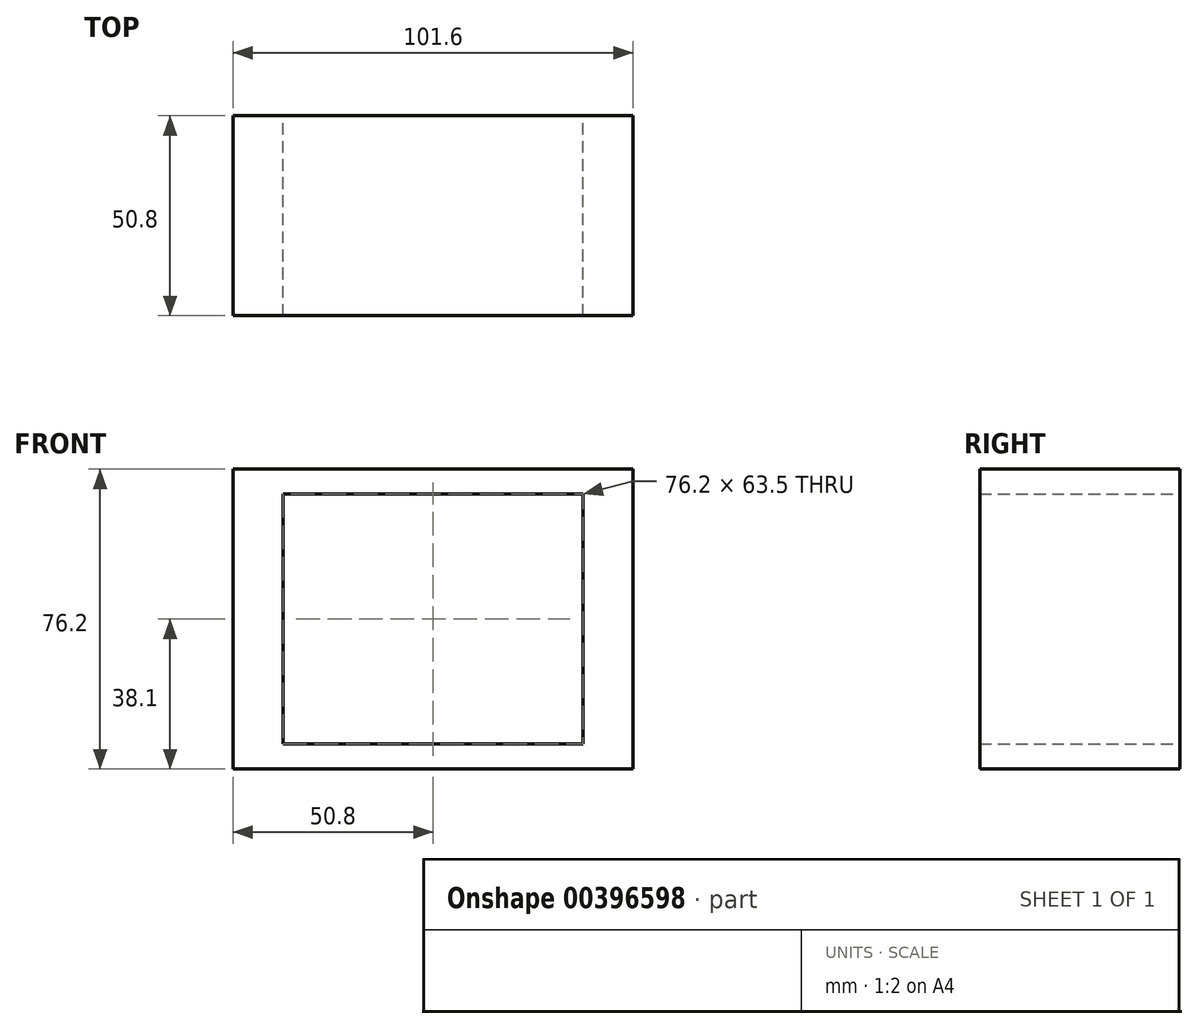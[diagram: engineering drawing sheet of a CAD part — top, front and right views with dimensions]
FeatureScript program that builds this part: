
annotation { "Feature Type Name" : "Feature", "Feature Type Description" : "" }
export const myFeature = defineFeature(function(context is Context, id is Id, definition is map)
    precondition{}
    {
        {
            var Q0;
            Q0=qCreatedBy(makeId("Front.planeOp"),FACE);
            var sketch = newSketch(context, id + "F0", { "sketchPlane" : qUnion([Q0])});
            skLineSegment(sketch, "E0.bottom", {"start": v(-50.8, 38.1) * mm, "end": v(50.8, 38.1) * mm});
            skLineSegment(sketch, "E0.top", {"start": v(-50.8, -38.1) * mm, "end": v(50.8, -38.1) * mm});
            skLineSegment(sketch, "E0.left", {"start": v(-50.8, 38.1) * mm, "end": v(-50.8, -38.1) * mm});
            skLineSegment(sketch, "E0.right", {"start": v(50.8, 38.1) * mm, "end": v(50.8, -38.1) * mm});
            skPoint(sketch, "E0.middle", {"position": v(0, 0) * mm});
            skLineSegment(sketch, "E1.bottom", {"start": v(-38.1, 31.75) * mm, "end": v(38.1, 31.75) * mm});
            skLineSegment(sketch, "E1.top", {"start": v(-38.1, -31.75) * mm, "end": v(38.1, -31.75) * mm});
            skLineSegment(sketch, "E1.left", {"start": v(-38.1, 31.75) * mm, "end": v(-38.1, -31.75) * mm});
            skLineSegment(sketch, "E1.right", {"start": v(38.1, 31.75) * mm, "end": v(38.1, -31.75) * mm});
            skSolve(sketch);
        }
        {
            var Q0;
            Q0=makeQuery(id+"F0.imprint","IMPRINT",FACE,{"disambiguationData":[TD([[makeQuery(id+"F0.imprint","IMPRINT",EDGE,{"derivedFrom":sQuery(id+"F0.wireOp",EDGE,"E0.bottom")}),-1.0]])]});
            extrude(context, id + "F1", {"entities" : qUnion([Q0]), "depth" : 50.8 * mm});
        }
    });
